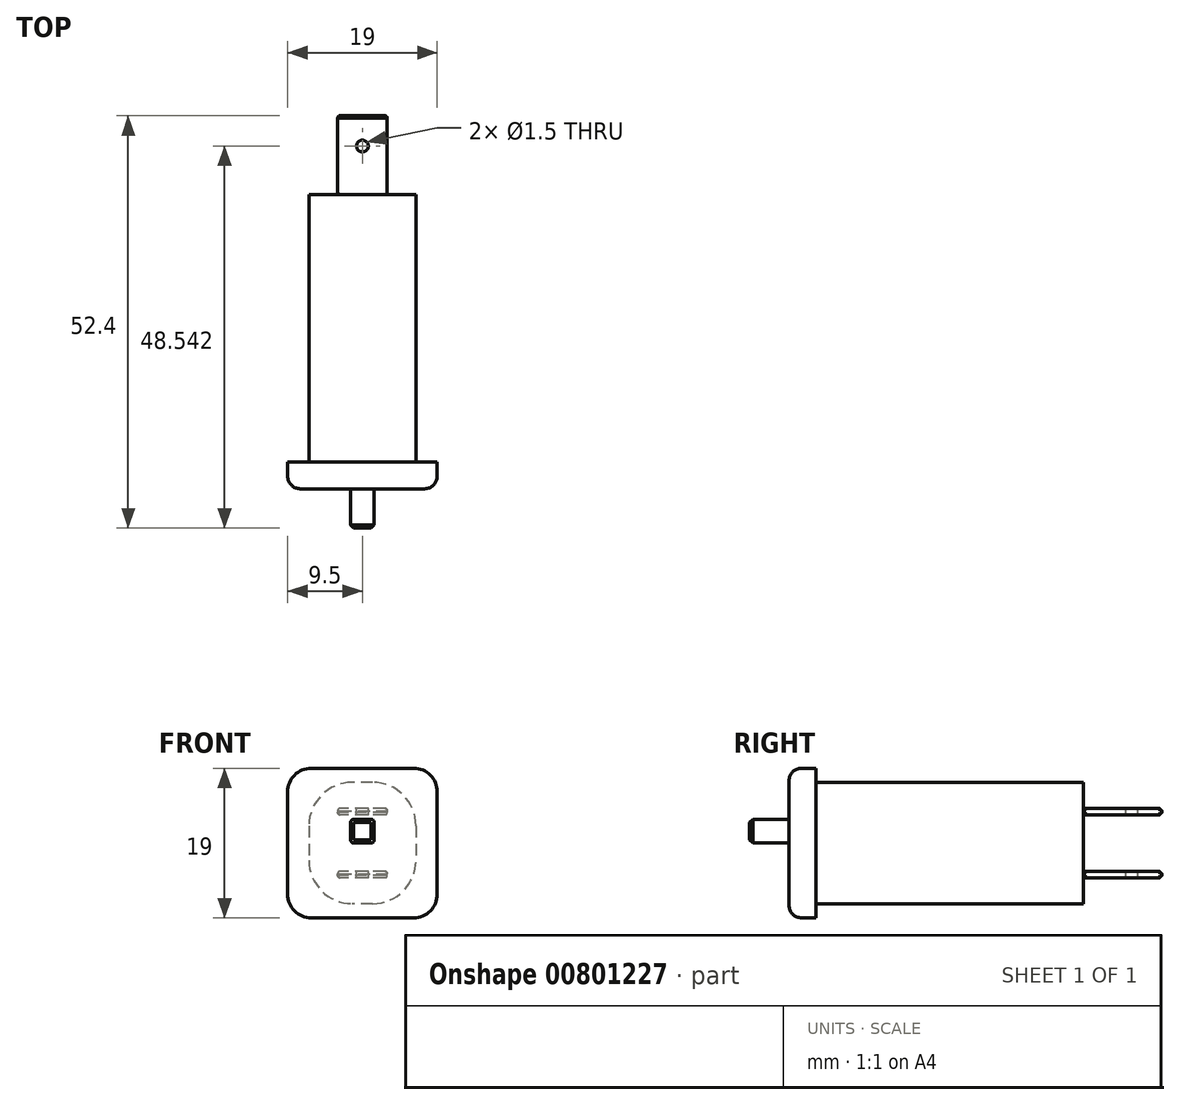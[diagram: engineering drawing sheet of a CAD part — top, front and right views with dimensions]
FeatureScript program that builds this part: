
annotation { "Feature Type Name" : "Feature", "Feature Type Description" : "" }
export const myFeature = defineFeature(function(context is Context, id is Id, definition is map)
    precondition{}
    {
        {
            var Q0;
            Q0=qCreatedBy(makeId("Right.planeOp"),FACE);
            var sketch = newSketch(context, id + "F0", { "sketchPlane" : qUnion([Q0])});
            skLineSegment(sketch, "E0.bottom", {"start": v(-17, 7.7) * mm, "end": v(17, 7.7) * mm});
            skLineSegment(sketch, "E0.top", {"start": v(-17, -7.7) * mm, "end": v(17, -7.7) * mm});
            skLineSegment(sketch, "E0.left", {"start": v(-17, 7.7) * mm, "end": v(-17, -7.7) * mm});
            skLineSegment(sketch, "E0.right", {"start": v(17, 7.7) * mm, "end": v(17, -7.7) * mm});
            skPoint(sketch, "E0.middle", {"position": v(0, 0) * mm});
            skLineSegment(sketch, "E1", {"start": v(30.15, 0) * mm, "end": v(-40.84, 0) * mm, "construction": true});
            skLineSegment(sketch, "E2.0", {"start": v(17, 3.6) * mm, "end": v(27, 3.6) * mm});
            skLineSegment(sketch, "E3.0", {"start": v(17, 4.4) * mm, "end": v(27, 4.4) * mm});
            skLineSegment(sketch, "E4", {"start": v(27, 4.4) * mm, "end": v(27, 3.6) * mm});
            skLineSegment(sketch, "E5", {"start": v(-17, 9.5) * mm, "end": v(-17, -9.5) * mm});
            skPoint(sketch, "E6", {"position": v(-17, 0) * mm});
            skLineSegment(sketch, "E7.0", {"start": v(-20.4, 9.5) * mm, "end": v(-20.4, -9.5) * mm});
            skLineSegment(sketch, "E8", {"start": v(-20.4, 9.5) * mm, "end": v(-17, 9.5) * mm});
            skLineSegment(sketch, "E9", {"start": v(-20.4, -9.5) * mm, "end": v(-17, -9.5) * mm});
            skLineSegment(sketch, "E10", {"start": v(-20.4, 0) * mm, "end": v(-25.4, 0) * mm});
            skLineSegment(sketch, "E11", {"start": v(-25.4, 0) * mm, "end": v(-25.4, 3) * mm});
            skLineSegment(sketch, "E12", {"start": v(-25.4, 3) * mm, "end": v(-20.4, 3) * mm});
            skLineSegment(sketch, "E13.MirrorCS", {"start": v(17, -3.6) * mm, "end": v(27, -3.6) * mm});
            skLineSegment(sketch, "E14.MirrorCS", {"start": v(17, -4.4) * mm, "end": v(27, -4.4) * mm});
            skLineSegment(sketch, "E15.MirrorCS", {"start": v(27, -4.4) * mm, "end": v(27, -3.6) * mm});
            skSolve(sketch);
        }
        {
            var Q0;
            {var subQ4=sQuery(id+"F0.wireOp",EDGE,"E0.bottom");Q0=makeQuery(id+"F0.imprint","IMPRINT",FACE,{"disambiguationData":[TD([[makeQuery(id+"F0.imprint","IMPRINT",EDGE,{"derivedFrom":subQ4}),-1.0]])]});}
            extrude(context, id + "F1", {"entities" : qUnion([Q0]), "depth" : 13.6 * mm, "offsetDistance" : 25 * mm, "symmetric" : true});
        }
        {
            var Q0;
            {var subQ3=sQuery(id+"F0.wireOp",EDGE,"E0.left");Q0=makeQuery(id+"F0.imprint","IMPRINT",FACE,{"disambiguationData":[TD([[makeQuery(id+"F0.imprint","IMPRINT",EDGE,{"derivedFrom":subQ3}),-1.0]])]});}
            extrude(context, id + "F2", {"entities" : qUnion([Q0]), "depth" : 19 * mm, "offsetDistance" : 25 * mm, "symmetric" : true});
        }
        {
            var Q0;
            {var subQ0=sQuery(id+"F0.wireOp",EDGE,"E10");Q0=makeQuery(id+"F0.imprint","IMPRINT",FACE,{"disambiguationData":[TD([[makeQuery(id+"F0.imprint","IMPRINT",EDGE,{"derivedFrom":subQ0}),-1.0]])]});}
            extrude(context, id + "F3", {"entities" : qUnion([Q0]), "depth" : 3 * mm, "offsetDistance" : 25 * mm, "symmetric" : true});
        }
        {
            var Q0;
            {var subQ0=sQuery(id+"F0.wireOp",EDGE,"E2.0");Q0=makeQuery(id+"F0.imprint","IMPRINT",FACE,{"disambiguationData":[TD([[makeQuery(id+"F0.imprint","IMPRINT",EDGE,{"derivedFrom":subQ0}),1.0]])]});}
            var Q1;
            {var subQ2=sQuery(id+"F0.wireOp",EDGE,"E13.MirrorCS");Q1=makeQuery(id+"F0.imprint","IMPRINT",FACE,{"disambiguationData":[TD([[makeQuery(id+"F0.imprint","IMPRINT",EDGE,{"derivedFrom":subQ2}),-1.0]])]});}
            extrude(context, id + "F4", {"entities" : qUnion([Q0, Q1]), "depth" : 6.3 * mm, "offsetDistance" : 25 * mm, "symmetric" : true});
        }
        {
            var Q0;
            Q0=makeQuery(id+"F1.opExtrude","CAP_EDGE",EDGE,{"disambiguationData":[OSD([sQuery(id+"F0.wireOp",EDGE,"E0.bottom")])],"isStart":false});
            var Q1;
            Q1=makeQuery(id+"F1.opExtrude","CAP_EDGE",EDGE,{"disambiguationData":[OSD([sQuery(id+"F0.wireOp",EDGE,"E0.bottom")])],"isStart":true});
            var Q2;
            Q2=makeQuery(id+"F1.opExtrude","CAP_EDGE",EDGE,{"disambiguationData":[OSD([sQuery(id+"F0.wireOp",EDGE,"E0.top")])],"isStart":false});
            var Q3;
            Q3=makeQuery(id+"F1.opExtrude","CAP_EDGE",EDGE,{"disambiguationData":[OSD([sQuery(id+"F0.wireOp",EDGE,"E0.top")])],"isStart":true});
            fillet(context, id + "F5", {"entities" : qUnion([Q0, Q1, Q2, Q3]), "tangentPropagation" : true, "radius" : 5.5 * mm, "defaultsChanged" : true, "vertexSettings" : [], "allowEdgeOverflow" : false});
        }
        {
            var Q0;
            Q0=makeQuery(id+"F2.opExtrude","CAP_EDGE",EDGE,{"disambiguationData":[OSD([sQuery(id+"F0.wireOp",EDGE,"E8")])],"isStart":false});
            var Q1;
            Q1=makeQuery(id+"F2.opExtrude","CAP_EDGE",EDGE,{"disambiguationData":[OSD([sQuery(id+"F0.wireOp",EDGE,"E8")])],"isStart":true});
            var Q2;
            Q2=makeQuery(id+"F2.opExtrude","CAP_EDGE",EDGE,{"disambiguationData":[OSD([sQuery(id+"F0.wireOp",EDGE,"E9")])],"isStart":false});
            var Q3;
            Q3=makeQuery(id+"F2.opExtrude","CAP_EDGE",EDGE,{"disambiguationData":[OSD([sQuery(id+"F0.wireOp",EDGE,"E9")])],"isStart":true});
            fillet(context, id + "F6", {"entities" : qUnion([Q0, Q1, Q2, Q3]), "tangentPropagation" : true, "radius" : 3 * mm, "defaultsChanged" : true, "vertexSettings" : [], "allowEdgeOverflow" : false});
        }
        {
            var Q0;
            Q0=makeQuery(id+"F2.opExtrude","SWEPT_EDGE",EDGE,{"disambiguationData":[OSD([sQuery(id+"F0.wireOp",EDGE,"E7.0"),sQuery(id+"F0.wireOp",EDGE,"E8")])]});
            var Q1;
            Q1=makeQuery(id+"F2.opExtrude","CAP_EDGE",EDGE,{"disambiguationData":[OSD([sQuery(id+"F0.wireOp",EDGE,"E7.0")])],"isStart":true});
            var Q2;
            Q2=makeQuery(id+"F2.opExtrude","SWEPT_EDGE",EDGE,{"disambiguationData":[OSD([sQuery(id+"F0.wireOp",EDGE,"E7.0"),sQuery(id+"F0.wireOp",EDGE,"E9")])]});
            var Q3;
            Q3=makeQuery(id+"F2.opExtrude","CAP_EDGE",EDGE,{"disambiguationData":[OSD([sQuery(id+"F0.wireOp",EDGE,"E7.0")])],"isStart":false});
            fillet(context, id + "F7", {"entities" : qUnion([Q0, Q1, Q2, Q3]), "tangentPropagation" : true, "radius" : 1.6 * mm, "defaultsChanged" : true, "vertexSettings" : [], "allowEdgeOverflow" : false});
        }
        {
            var Q0;
            Q0=makeQuery(id+"F3.opExtrude","CAP_EDGE",EDGE,{"disambiguationData":[OSD([sQuery(id+"F0.wireOp",EDGE,"E12")])],"isStart":false});
            var Q1;
            Q1=makeQuery(id+"F3.opExtrude","CAP_EDGE",EDGE,{"disambiguationData":[OSD([sQuery(id+"F0.wireOp",EDGE,"E10")])],"isStart":false});
            var Q2;
            Q2=makeQuery(id+"F3.opExtrude","CAP_EDGE",EDGE,{"disambiguationData":[OSD([sQuery(id+"F0.wireOp",EDGE,"E12")])],"isStart":true});
            var Q3;
            Q3=makeQuery(id+"F3.opExtrude","CAP_EDGE",EDGE,{"disambiguationData":[OSD([sQuery(id+"F0.wireOp",EDGE,"E10")])],"isStart":true});
            fillet(context, id + "F8", {"entities" : qUnion([Q0, Q1, Q2, Q3]), "tangentPropagation" : true, "radius" : 0.4 * mm, "defaultsChanged" : true, "vertexSettings" : [], "allowEdgeOverflow" : false});
        }
        {
            var Q0;
            Q0=makeQuery(id+"F3.opExtrude","SWEPT_EDGE",EDGE,{"disambiguationData":[OSD([sQuery(id+"F0.wireOp",EDGE,"E11"),sQuery(id+"F0.wireOp",EDGE,"E12")])]});
            var Q1;
            Q1=makeQuery(id+"F3.opExtrude","SWEPT_EDGE",EDGE,{"disambiguationData":[OSD([sQuery(id+"F0.wireOp",EDGE,"E10"),sQuery(id+"F0.wireOp",EDGE,"E11")])]});
            var Q2;
            Q2=makeQuery(id+"F3.opExtrude","CAP_EDGE",EDGE,{"disambiguationData":[OSD([sQuery(id+"F0.wireOp",EDGE,"E11")])],"isStart":true});
            var Q3;
            Q3=makeQuery(id+"F3.opExtrude","CAP_EDGE",EDGE,{"disambiguationData":[OSD([sQuery(id+"F0.wireOp",EDGE,"E11")])],"isStart":false});
            chamfer(context, id + "F9", {"entities" : qUnion([Q0, Q1, Q2, Q3]), "width" : 0.4 * mm, "tangentPropagation" : true});
        }
        {
            var Q0;
            Q0=makeQuery(id+"F4.opExtrude","CAP_FACE",FACE,{"disambiguationData":[OSD([sQuery(id+"F0.wireOp",EDGE,"E0.right"),sQuery(id+"F0.wireOp",EDGE,"E13.MirrorCS"),sQuery(id+"F0.wireOp",EDGE,"E14.MirrorCS"),sQuery(id+"F0.wireOp",EDGE,"E15.MirrorCS")])],"isStart":false});
            var Q1;
            Q1=makeQuery(id+"F4.opExtrude","CAP_FACE",FACE,{"disambiguationData":[OSD([sQuery(id+"F0.wireOp",EDGE,"E0.right"),sQuery(id+"F0.wireOp",EDGE,"E2.0"),sQuery(id+"F0.wireOp",EDGE,"E3.0"),sQuery(id+"F0.wireOp",EDGE,"E4")])],"isStart":false});
            var Q2;
            Q2=makeQuery(id+"F4.opExtrude","CAP_FACE",FACE,{"disambiguationData":[OSD([sQuery(id+"F0.wireOp",EDGE,"E0.right"),sQuery(id+"F0.wireOp",EDGE,"E13.MirrorCS"),sQuery(id+"F0.wireOp",EDGE,"E14.MirrorCS"),sQuery(id+"F0.wireOp",EDGE,"E15.MirrorCS")])],"isStart":true});
            var Q3;
            Q3=makeQuery(id+"F4.opExtrude","CAP_FACE",FACE,{"disambiguationData":[OSD([sQuery(id+"F0.wireOp",EDGE,"E0.right"),sQuery(id+"F0.wireOp",EDGE,"E2.0"),sQuery(id+"F0.wireOp",EDGE,"E3.0"),sQuery(id+"F0.wireOp",EDGE,"E4")])],"isStart":true});
            fillet(context, id + "F10", {"entities" : qUnion([Q0, Q1, Q2, Q3]), "tangentPropagation" : true, "radius" : 0.3 * mm, "defaultsChanged" : false, "vertexSettings" : [], "allowEdgeOverflow" : false});
        }
        {
            var Q0;
            Q0=makeQuery(id+"F4.opExtrude","SWEPT_EDGE",EDGE,{"disambiguationData":[OSD([sQuery(id+"F0.wireOp",EDGE,"E3.0"),sQuery(id+"F0.wireOp",EDGE,"E4")])]});
            var Q1;
            Q1=makeQuery(id+"F4.opExtrude","SWEPT_EDGE",EDGE,{"disambiguationData":[OSD([sQuery(id+"F0.wireOp",EDGE,"E2.0"),sQuery(id+"F0.wireOp",EDGE,"E4")])]});
            var Q2;
            Q2=makeQuery(id+"F4.opExtrude","SWEPT_EDGE",EDGE,{"disambiguationData":[OSD([sQuery(id+"F0.wireOp",EDGE,"E13.MirrorCS"),sQuery(id+"F0.wireOp",EDGE,"E15.MirrorCS")])]});
            var Q3;
            Q3=makeQuery(id+"F4.opExtrude","SWEPT_EDGE",EDGE,{"disambiguationData":[OSD([sQuery(id+"F0.wireOp",EDGE,"E14.MirrorCS"),sQuery(id+"F0.wireOp",EDGE,"E15.MirrorCS")])]});
            chamfer(context, id + "F11", {"entities" : qUnion([Q0, Q1, Q2, Q3]), "width" : 0.3 * mm, "tangentPropagation" : true});
        }
        {
            var Q0;
            Q0=makeQuery(id+"F4.opExtrude","SWEPT_FACE",FACE,{"disambiguationData":[OSD([sQuery(id+"F0.wireOp",EDGE,"E3.0")])]});
            var sketch = newSketch(context, id + "F12", { "sketchPlane" : qUnion([Q0])});
            skCircle(sketch, "E16", {"center": v(0, 23.14) * mm, "radius": 0.75 * mm});
            skPoint(sketch, "E16.centerSnap0", {"position": v(0, 17) * mm});
            skSolve(sketch);
        }
        {
            var Q0;
            Q0=makeQuery(id+"F12.imprint","IMPRINT",FACE,{"disambiguationData":[TD([[makeQuery(id+"F12.imprint","IMPRINT",EDGE,{"derivedFrom":sQuery(id+"F12.wireOp",EDGE,"E16")}),1.0]])]});
            extrude(context, id + "F13", {"entities" : qUnion([Q0]), "operationType" : NewBodyOperationType.REMOVE, "oppositeDirection" : true, "depth" : 10 * mm, "offsetDistance" : 25 * mm});
        }
    });
